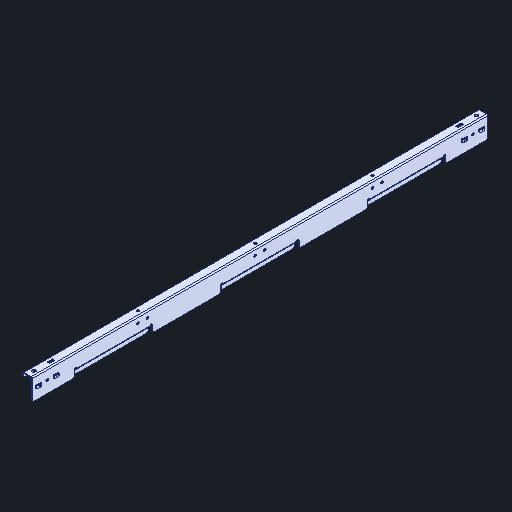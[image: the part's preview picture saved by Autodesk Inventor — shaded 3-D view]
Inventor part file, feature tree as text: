
AUTODESK INVENTOR PART (.ipt)
format: ipt  version: 2024 (Build 280153000, 153)  size: 236,032 bytes
history: native  units: in
note: dims shown in document units (in); Inventor stores cm internally (conversion verified against a paired STEP export)
features: fillet x1
ambient origin geometry x8: Origin, YZ Plane, XZ Plane, XY Plane, X Axis, Y Axis, Z Axis, Center Point
bodies: Solid1 (feature_tree)
feature tree (1):
  fillet  "Fillet1"  [1 undecoded]
note: 1 required parameter value undecoded (feature->parameter linkage not recoverable at this tier; creation-order binding heuristic only, values carry confidence <= 0.55)
